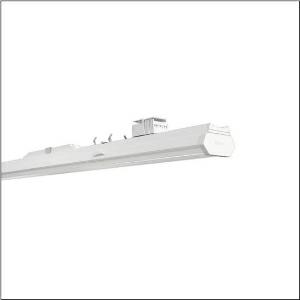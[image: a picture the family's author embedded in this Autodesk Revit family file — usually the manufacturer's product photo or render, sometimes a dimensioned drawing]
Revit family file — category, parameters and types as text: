
# Revit family: licross_r__11_protected_ho_51tp12dn4fxmd_e40f
name_source: partatom
category: Lighting Fixtures
units: mm (PartAtom-declared; Revit-internal decimal feet)

## family parameters
Cut with Voids When Loaded = No
Host = Face
Light Source = No
Part Type = Normal
Room Calculation Point = No
Round Connector Dimension = Use Diameter
Shared = No

## types (1)
- --- (1 x LED, 2290 lm, 13.9 W, 4000K)
    Apparent Load = 14 VA
    CIE Flux Codes = 70 91 97 98 100
    Color Rendering = 80
    Color Temperature = 4000K
    Default Elevation = 1800 mm
    Description = Licross® 11 Protected HO, luminaire insert, of sheet steel, galvanised, coil coated, white, length: 1.500mm, width: 90mm, height: 101mm, LED rated luminous flux: 15.270lm, light colour: 840, control gear: DALI 2 (for two DALI lines), with plug, 6-pole, with phase selection, mains connection: 220..240V, AC/DC, 0/50..60Hz, rated input power: 87W, internal wiring halogen-free, for central battery installations according to DIN EN 60598-2-22, for emergency light function, without changeover relay, primary optical cover: cover, of PMMA, light emission: direct distribution, primary light characteristic: symmetric, protection rating (complete): IP64, insulation class (complete): insulation class I (protective earthing), certification: CE, ENEC, VDE, UKCA, protection symbol: D if used in an environment with conductive dust loads with corresponding accessories, impact resistance: IK06, permissible ambient temperature for indoor applications: -25..+30°C, standard: EN 60598-2-22, corresponds to IFS (International Featured Standards) requirements for safety and quality in the food industry, reducing of maximum allowable ambient temperature of 5°C with ceiling mounting, LABS conformity tested according to VDMA 24364:2018-05, packaging unit: 1 piece
    Height = 92 mm
    Lamp = 1 x LED
    Lamp Light Flux = 2290 lm
    Lamp Power = 13.9 W
    Lamp count = 1
    Length = 1500 mm
    Luminous efficacy = 165 lm/W
    Manufacturer = Siteco
    ModVariant = No
    Model = 51TP12DN4FXMD
    Mounting Place = Ceiling
    Mounting Type = Pendant
    Number of Poles = 1
    OnlyDefault = Yes
    Power Factor = 1
    Product Name = Licross® 11 Protected HO
    Product group = luminaire insert | ceiling pendant
    ProductGroupID = 902
    Protection Class = Protection class I
    Protection Degree = IP 64
    RLX_Detail_Level = 1
    RLX_Emergency_Light_Flux = 0 lm
    RLX_Emergency_Type = 0
    RLX_Emergency_Type_DB = No
    RlxData = <blob elided: 24885 chars, md5=c56e8140>
    Socket = socket
    Standby Power = 0 W
    System Light Flux = 2290 lm
    System Power = 14 W
    Type Comments = : DC mode (central or group accumulator) initial emergency light level
    Type Image = l_1256148.jpg
    URL = http://relux.com
    VarID = @adj_109159
    Voltage = 0 V
    Weight = 0.00 kg
    Width = 88 mm

## geometry (parser evidence)
native form markers: Blend x4, Sweep x12
no freeform markers — native parametric forms only
